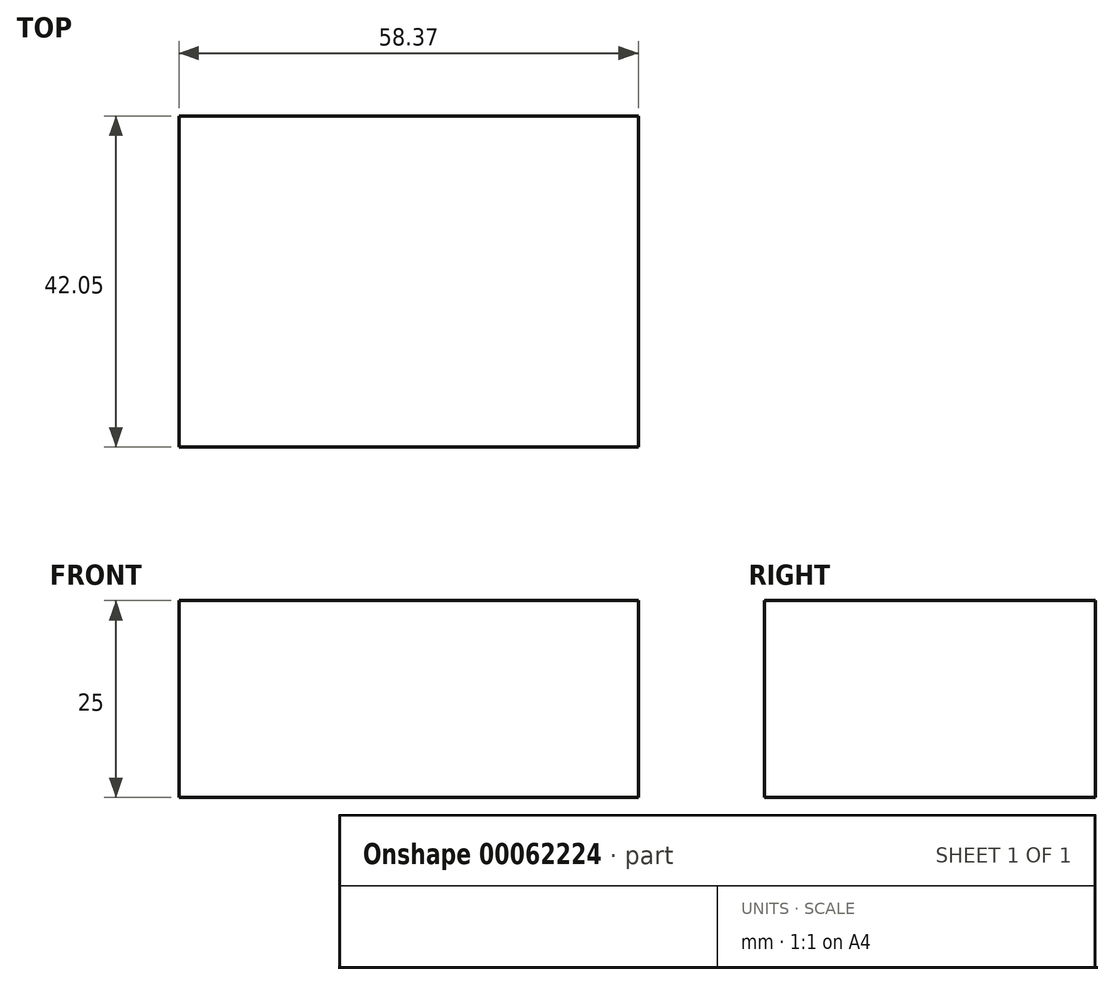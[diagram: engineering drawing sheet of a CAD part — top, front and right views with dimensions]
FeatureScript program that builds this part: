
annotation { "Feature Type Name" : "Feature", "Feature Type Description" : "" }
export const myFeature = defineFeature(function(context is Context, id is Id, definition is map)
    precondition{}
    {
        {
            var Q0;
            Q0=qCreatedBy(makeId("Top.planeOp"),FACE);
            var sketch = newSketch(context, id + "F0", { "sketchPlane" : qUnion([Q0])});
            skLineSegment(sketch, "E0.bottom", {"start": v(-83.87, -16.7) * mm, "end": v(-25.5, -16.7) * mm});
            skLineSegment(sketch, "E0.top", {"start": v(-83.87, -58.75) * mm, "end": v(-25.5, -58.75) * mm});
            skLineSegment(sketch, "E0.left", {"start": v(-83.87, -16.7) * mm, "end": v(-83.87, -58.75) * mm});
            skLineSegment(sketch, "E0.right", {"start": v(-25.5, -16.7) * mm, "end": v(-25.5, -58.75) * mm});
            skSolve(sketch);
        }
        {
            var Q0;
            Q0=qSketchRegion(id+"F0",true);
            extrude(context, id + "F1", {"entities" : qUnion([Q0]), "depth" : 25 * mm});
        }
    });
